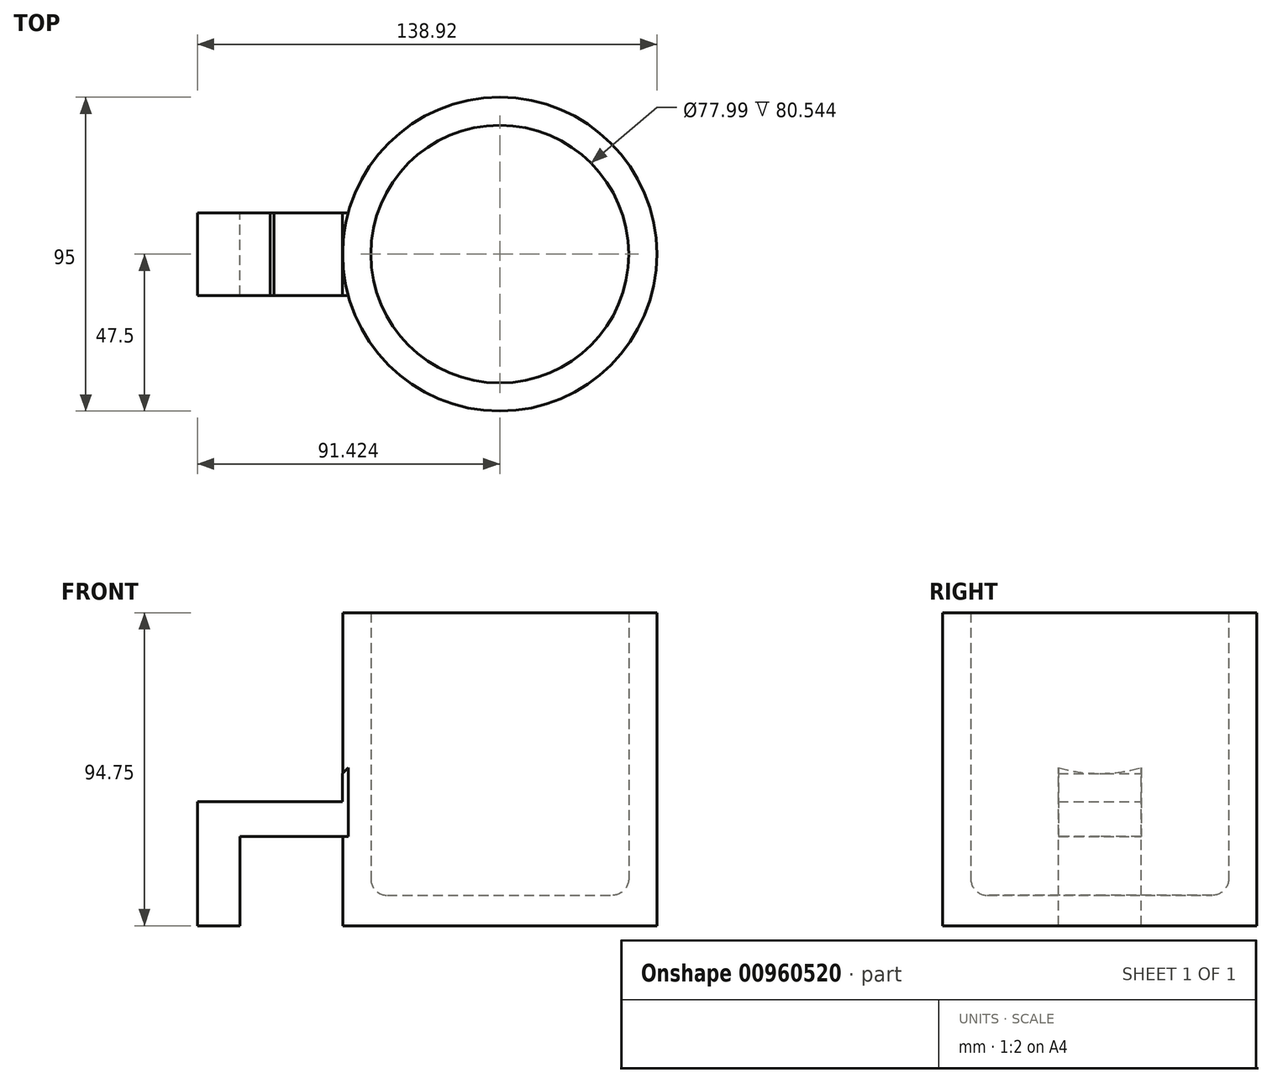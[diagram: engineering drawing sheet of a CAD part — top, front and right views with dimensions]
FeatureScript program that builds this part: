
annotation { "Feature Type Name" : "Feature", "Feature Type Description" : "" }
export const myFeature = defineFeature(function(context is Context, id is Id, definition is map)
    precondition{}
    {
        {
            var Q0;
            Q0=qCreatedBy(makeId("Front.planeOp"),FACE);
            var sketch = newSketch(context, id + "F0", { "sketchPlane" : qUnion([Q0])});
            skLineSegment(sketch, "E0", {"start": v(-25.43, -60.7) * mm, "end": v(-25.43, -33.7) * mm});
            skLineSegment(sketch, "E1", {"start": v(-25.43, -33.7) * mm, "end": v(14.07, -33.7) * mm});
            skLineSegment(sketch, "E2", {"start": v(5.57, -33.7) * mm, "end": v(5.57, -60.7) * mm});
            skLineSegment(sketch, "E3", {"start": v(5.57, -60.7) * mm, "end": v(100.57, -60.7) * mm});
            skLineSegment(sketch, "E4", {"start": v(100.57, -60.7) * mm, "end": v(100.57, 34.05) * mm});
            skLineSegment(sketch, "E5", {"start": v(-25.43, -60.7) * mm, "end": v(-38.35, -60.7) * mm});
            skLineSegment(sketch, "E6", {"start": v(-38.35, -60.7) * mm, "end": v(-38.35, -23.2) * mm});
            skLineSegment(sketch, "E7", {"start": v(-38.35, -23.2) * mm, "end": v(5.57, -23.2) * mm});
            skLineSegment(sketch, "E8", {"start": v(14.07, -23.18) * mm, "end": v(14.07, -46.5) * mm});
            skLineSegment(sketch, "E9", {"start": v(19.07, -51.5) * mm, "end": v(87.07, -51.5) * mm});
            skLineSegment(sketch, "E10", {"start": v(92.07, -46.5) * mm, "end": v(92.07, 34.05) * mm});
            skLineSegment(sketch, "E11", {"start": v(92.07, 34.05) * mm, "end": v(100.57, 34.05) * mm});
            skPoint(sketch, "E12", {"position": v(53.07, -51.5) * mm});
            skLineSegment(sketch, "E13", {"start": v(14.07, -33.7) * mm, "end": v(14.07, 28.5) * mm});
            skLineSegment(sketch, "E14", {"start": v(53.07, -60.7) * mm, "end": v(53.07, 29.62) * mm});
            skPoint(sketch, "E15.visualSharp", {"position": v(92.07, -51.5) * mm});
            skArc(sketch, "E15.filletArc", {"start": v(87.07, -51.5) * mm, "mid": v(90.6, -50.03) * mm, "end": v(92.07, -46.5) * mm});
            skPoint(sketch, "E16.visualSharp", {"position": v(14.07, -51.5) * mm});
            skArc(sketch, "E16.filletArc", {"start": v(14.07, -46.5) * mm, "mid": v(15.54, -50.03) * mm, "end": v(19.07, -51.5) * mm});
            skLineSegment(sketch, "E17", {"start": v(5.57, -23.2) * mm, "end": v(5.57, 28.5) * mm});
            skLineSegment(sketch, "E18", {"start": v(5.57, 28.5) * mm, "end": v(14.07, 28.5) * mm});
            skArc(sketch, "E19", {"start": v(-16.4, -23.2) * mm, "mid": v(2.88, -16.9) * mm, "end": v(14.07, 0) * mm});
            skLineSegment(sketch, "E20", {"start": v(5.57, -23.2) * mm, "end": v(14.07, -23.18) * mm});
            skSolve(sketch);
        }
        {
            var Q0;
            {var subQ6=sQuery(id+"F0.wireOp",EDGE,"E4");Q0=makeQuery(id+"F0.imprint","IMPRINT",FACE,{"disambiguationData":[TD([[makeQuery(id+"F0.imprint","IMPRINT",EDGE,{"derivedFrom":subQ6}),1.0]])]});}
            var Q1;
            Q1=sQuery(id+"F0.wireOp",EDGE,"E14");
            revolve(context, id + "F1", {"surfaceOperationType" : NewSurfaceOperationType.NEW, "entities" : qUnion([Q0]), "axis" : qUnion([Q1]), "revolveType" : RevolveType.FULL});
        }
        {
            var Q0;
            {var subQ5=sQuery(id+"F0.wireOp",EDGE,"E0");Q0=makeQuery(id+"F0.imprint","IMPRINT",FACE,{"disambiguationData":[TD([[makeQuery(id+"F0.imprint","IMPRINT",EDGE,{"derivedFrom":subQ5}),1.0]])]});}
            var Q1;
            {var subQ0=sQuery(id+"F0.wireOp",EDGE,"E19");var subQ1=sQuery(id+"F0.wireOp",EDGE,"E7");var subQ2=makeQuery(id+"F0.imprint","INTERSECT",VERTEX,{"disambiguationData":[OD(0.0)],"derivedFrom":[subQ1,subQ0]});Q1=makeQuery(id+"F0.imprint","IMPRINT",FACE,{"disambiguationData":[TD([[makeQuery(id+"F0.imprint","IMPRINT",EDGE,{"disambiguationData":[TD([[subQ2,-1.0]])],"derivedFrom":subQ0}),-1.0]])]});}
            var Q2;
            {var subQ3=sQuery(id+"F0.wireOp",EDGE,"E20");Q2=makeQuery(id+"F0.imprint","IMPRINT",FACE,{"disambiguationData":[TD([[makeQuery(id+"F0.imprint","IMPRINT",EDGE,{"derivedFrom":subQ3}),1.0]])]});}
            extrude(context, id + "F2", {"entities" : qUnion([Q0, Q1, Q2]), "operationType" : NewBodyOperationType.ADD, "endBound" : BoundingType.SYMMETRIC, "depth" : 25 * mm, "offsetDistance" : 25 * mm});
        }
    });
